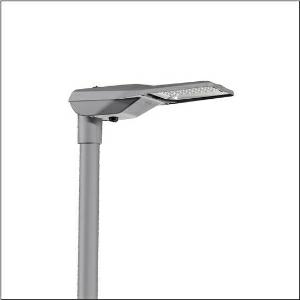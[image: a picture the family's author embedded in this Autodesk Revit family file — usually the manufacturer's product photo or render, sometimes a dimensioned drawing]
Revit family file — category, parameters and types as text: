
# Revit family: streetlight_sl_21_iq_mini___p0_5a_5xe2v31y08jb_f279
name_source: partatom
category: Lighting Fixtures
units: mm (PartAtom-declared; Revit-internal decimal feet)

## family parameters
Cut with Voids When Loaded = No
Host = Face
Light Source = No
Part Type = Normal
Room Calculation Point = No
Round Connector Dimension = Use Diameter
Shared = No

## types (1)
- --- (1 x LED, 11020 lm, 72.5 W, 3000K)
    Apparent Load = 73 VA
    CIE Flux Codes = 37 73 96 100 100
    Color Rendering = 70
    Color Temperature = 3000K
    Default Elevation = 1800 mm
    Description = Streetlight SL 21 iQ mini, mast luminaire, primary light control with lens, of PMMA, primary optical cover: cover, of toughened safety glass, transparent, light distribution: P0.5a, light emission: direct distribution, primary light characteristic: asymmetric, installation type: post-top, side-entry, LED, High Power LED, rated luminous flux: 11.020lm, luminous efficacy: 152lm/W, light colour: 730, colour temperature: 3000K, control gear: iQ-Street Remote, D4i with power reduction, control: pre-setting: logarithmic dimming characteristic, Street-Remote, Auto-Match, Temp-Guard, Lumen-Switch, Night-Set, Smart-Wire, Light-Fading, Desk-Remote (wireless, voltage-free reading and setting of iQ features in the workshop via application-optimized NFC function/RFID function), optimised constant luminous flux control (CLO 2.0), mains connection: 220..240V, AC, 50/60Hz, start of lifetime: 73W, end of service life: 76W, reduction: 33W, luminaire housing, of diecast aluminium, powder-coated, Siteco® metallic grey (DB 702S), corrosivity category C5 mid according to DIN EN ISO 12944, please order mast flange separately, inclination adjustable: 0°, 5°, 10°, 15°, sealing non-destructively replaceable, multi-level sealing system, length: 628mm, width: 235mm, height: 110mm, mast flange for spigot size: 42mm (side-entry): 5XC10008XM4, 60/48mm (side-entry/post-top): 5XC10108XM2, 76/60mm (side-entry/post-top): 5XC10108XM1, mounting height: 4..8m, Smart Interface below and above, protection rating (complete): IP66, insulation class (complete): insulation class II (safety insulation), certification: CE, ENEC, ENEC+, VDE, impact resistance: IK10, permissible operating ambient temperature for outdoor applications: -40..+50°C, standard-compliant lighting for roads and squares, packaging unit: 1 piece

Light Distribution: P0.5a
    Height = 110 mm
    Lamp = 1 x LED
    Lamp Light Flux = 11020 lm
    Lamp Power = 72.5 W
    Lamp count = 1
    Length = 625 mm
    Luminous efficacy = 152 lm/W
    Manufacturer = Siteco
    ModVariant = No
    Model = 5XE2V31Y08JB
    Number of Poles = 1
    OnlyDefault = Yes
    Power Factor = 1
    Product Name = Streetlight SL 21 iQ mini | P0.5a
    Product group = mast luminaire | pylon top
    ProductGroupID = 6100
    Protection Class = Protection class II
    Protection Degree = IP 66
    RLX_Detail_Level = 1
    RLX_Emergency_Light_Flux = 0 lm
    RLX_Emergency_Type = 0
    RLX_Emergency_Type_DB = No
    RlxData = <blob elided: 26353 chars, md5=08921e48>
    Socket = socket
    Standby Power = 0 W
    System Light Flux = 11020 lm
    System Power = 73 W
    Type Comments = factory setting: luminous flux: 100 % | dim-lin: 254 | 755 mA
    Type Image = l_1003514.jpg
    URL = http://relux.com
    VarID = @adj_069388
    Voltage = 0 V
    Weight = 0.00 kg
    Width = 234 mm

## geometry (parser evidence)
native form markers: Blend x4, Sweep x11
no freeform markers — native parametric forms only
